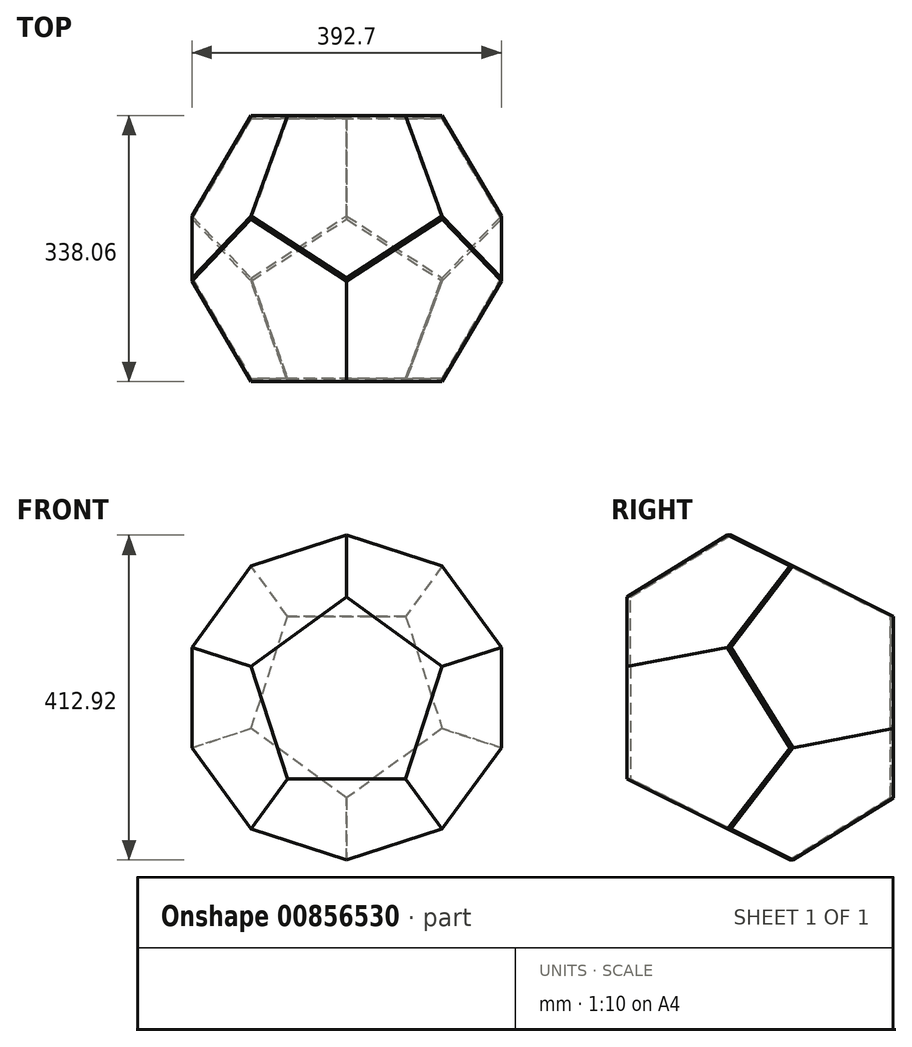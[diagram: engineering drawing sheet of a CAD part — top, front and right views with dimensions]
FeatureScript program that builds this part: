
annotation { "Feature Type Name" : "Feature", "Feature Type Description" : "" }
export const myFeature = defineFeature(function(context is Context, id is Id, definition is map)
    precondition{}
    {
        {
            var Q0;
            Q0=qCreatedBy(makeId("Front.planeOp"),FACE);
            var sketch = newSketch(context, id + "F0", { "sketchPlane" : qUnion([Q0])});
            skLineSegment(sketch, "E0", {"start": v(0, -103.23) * mm, "end": v(0, 127.6) * mm, "construction": true});
            skLineSegment(sketch, "E1", {"start": v(75, -103.23) * mm, "end": v(-75, -103.23) * mm});
            skLineSegment(sketch, "E2", {"start": v(0, -103.23) * mm, "end": v(0, 0) * mm, "construction": true});
            skLineSegment(sketch, "E3.1.0", {"start": v(121.35, 39.43) * mm, "end": v(75, -103.23) * mm});
            skLineSegment(sketch, "E3.2.0", {"start": v(0, 127.6) * mm, "end": v(121.35, 39.43) * mm});
            skLineSegment(sketch, "E3.3.0", {"start": v(-121.35, 39.43) * mm, "end": v(0, 127.6) * mm});
            skLineSegment(sketch, "E3.4.0", {"start": v(-75, -103.23) * mm, "end": v(-121.35, 39.43) * mm});
            skPoint(sketch, "E3.center", {"position": v(0, 0) * mm});
            skLineSegment(sketch, "E4", {"start": v(-121.35, 39.43) * mm, "end": v(98.18, -31.9) * mm, "construction": true});
            skLineSegment(sketch, "E5", {"start": v(-75, -103.23) * mm, "end": v(60.68, 83.51) * mm, "construction": true});
            skLineSegment(sketch, "E6", {"start": v(-60.68, 83.51) * mm, "end": v(75, -103.23) * mm, "construction": true});
            skLineSegment(sketch, "E7", {"start": v(121.35, 39.43) * mm, "end": v(-98.18, -31.9) * mm, "construction": true});
            skLineSegment(sketch, "E8.bottom", {"start": v(-75, -103.23) * mm, "end": v(75, -103.23) * mm, "construction": true});
            skLineSegment(sketch, "E8.top", {"start": v(-75, 103.23) * mm, "end": v(75, 103.23) * mm, "construction": true});
            skLineSegment(sketch, "E8.left", {"start": v(-75, -103.23) * mm, "end": v(-75, 103.23) * mm, "construction": true});
            skLineSegment(sketch, "E8.right", {"start": v(75, -103.23) * mm, "end": v(75, 103.23) * mm, "construction": true});
            skSolve(sketch);
        }
        {
            var Q0;
            Q0=qCreatedBy(makeId("Right.planeOp"),FACE);
            var sketch = newSketch(context, id + "F1", { "sketchPlane" : qUnion([Q0])});
            skLineSegment(sketch, "E9", {"start": v(0, -103.23) * mm, "end": v(60.48, -133.47) * mm, "construction": true});
            skSolve(sketch);
        }
        {
            var Q0;
            Q0=sQuery(id+"F1.wireOp",EDGE,"E9");
            var Q1;
            Q1=sQuery(id+"F0.wireOp",EDGE,"E1");
            cPlane(context, id + "F2", {"entities" : qUnion([Q0, Q1]), "cplaneType" : CPlaneType.LINE_ANGLE, "offset" : 25 * mm, "angle" : 0 * degree, "width" : 150 * mm, "height" : 150 * mm});
        }
        {
            var Q0;
            Q0=qCreatedBy(id+"F2.planeOp",FACE);
            var sketch = newSketch(context, id + "F3", { "sketchPlane" : qUnion([Q0])});
            skLineSegment(sketch, "E10.0", {"start": v(75, 46.17) * mm, "end": v(-75, 46.17) * mm});
            skLineSegment(sketch, "E11.1.0", {"start": v(121.35, 188.82) * mm, "end": v(75, 46.17) * mm});
            skLineSegment(sketch, "E11.2.0", {"start": v(0, 277) * mm, "end": v(121.35, 188.82) * mm});
            skLineSegment(sketch, "E11.3.0", {"start": v(-121.35, 188.82) * mm, "end": v(0, 277) * mm});
            skLineSegment(sketch, "E11.4.0", {"start": v(-75, 46.17) * mm, "end": v(-121.35, 188.82) * mm});
            skPoint(sketch, "E11.center", {"position": v(0, 149.4) * mm});
            skSolve(sketch);
        }
        {
            var Q0;
            Q0=sQuery(id+"F0.wireOp",EDGE,"E3.1.0");
            cPlane(context, id + "F4", {"entities" : qUnion([Q0]), "cplaneType" : CPlaneType.LINE_ANGLE, "offset" : 25 * mm, "angle" : 206.56 * degree, "width" : 150 * mm, "height" : 150 * mm});
        }
        {
            var Q0;
            Q0=qCreatedBy(id+"F4.planeOp",FACE);
            var sketch = newSketch(context, id + "F5", { "sketchPlane" : qUnion([Q0])});
            skLineSegment(sketch, "E12.0", {"start": v(46.17, 75) * mm, "end": v(46.17, -75) * mm});
            skLineSegment(sketch, "E13.1.0", {"start": v(46.17, -75) * mm, "end": v(188.82, -121.35) * mm});
            skLineSegment(sketch, "E13.2.0", {"start": v(188.82, -121.35) * mm, "end": v(277, 0) * mm});
            skLineSegment(sketch, "E13.3.0", {"start": v(277, 0) * mm, "end": v(188.82, 121.35) * mm});
            skLineSegment(sketch, "E13.4.0", {"start": v(188.82, 121.35) * mm, "end": v(46.17, 75) * mm});
            skPoint(sketch, "E13.center", {"position": v(149.4, 0) * mm});
            skSolve(sketch);
        }
        {
            var Q0;
            Q0=sQuery(id+"F0.wireOp",EDGE,"E3.2.0");
            var Q1;
            Q1=qCreatedBy(id+"FWBOnNek9pfn1HW_0.planeOp",FACE);
            cPlane(context, id + "F6", {"entities" : qUnion([Q0, Q1]), "cplaneType" : CPlaneType.LINE_ANGLE, "offset" : 25 * mm, "angle" : 116.56 * degree, "width" : 150 * mm, "height" : 150 * mm});
        }
        {
            var Q0;
            Q0=qCreatedBy(id+"F6.planeOp",FACE);
            var sketch = newSketch(context, id + "F7", { "sketchPlane" : qUnion([Q0])});
            skLineSegment(sketch, "E14.0", {"start": v(-57.06, 67.08) * mm, "end": v(85.6, 20.73) * mm});
            skLineSegment(sketch, "E15.1.0", {"start": v(85.6, 20.73) * mm, "end": v(173.76, 142.08) * mm});
            skLineSegment(sketch, "E15.2.0", {"start": v(173.76, 142.08) * mm, "end": v(85.6, 263.43) * mm});
            skLineSegment(sketch, "E15.3.0", {"start": v(85.6, 263.43) * mm, "end": v(-57.06, 217.08) * mm});
            skLineSegment(sketch, "E15.4.0", {"start": v(-57.06, 217.08) * mm, "end": v(-57.06, 67.08) * mm});
            skPoint(sketch, "E15.center", {"position": v(46.17, 142.08) * mm});
            skSolve(sketch);
        }
        {
            var Q0;
            Q0=sQuery(id+"F0.wireOp",VERTEX,"E1.end");
            var Q1;
            Q1=sQuery(id+"F3.wireOp",VERTEX,"E11.3.0.start");
            var Q2;
            Q2=sQuery(id+"F0.wireOp",VERTEX,"E3.3.0.start");
            cPlane(context, id + "F8", {"entities" : qUnion([Q0, Q1, Q2]), "cplaneType" : CPlaneType.THREE_POINT, "offset" : 25 * mm, "width" : 150 * mm, "height" : 150 * mm});
        }
        {
            var Q0;
            Q0=sQuery(id+"F0.wireOp",VERTEX,"E0.end");
            var Q1;
            Q1=sQuery(id+"F0.wireOp",VERTEX,"E3.3.0.start");
            var Q2;
            Q2=sQuery(id+"F7.wireOp",VERTEX,"E15.3.0.end");
            cPlane(context, id + "F9", {"entities" : qUnion([Q0, Q1, Q2]), "cplaneType" : CPlaneType.THREE_POINT, "offset" : 25 * mm, "width" : 150 * mm, "height" : 150 * mm});
        }
        {
            var Q0;
            Q0=qCreatedBy(id+"F8.planeOp",FACE);
            var sketch = newSketch(context, id + "F10", { "sketchPlane" : qUnion([Q0])});
            skLineSegment(sketch, "E16.0", {"start": v(-46.17, -75) * mm, "end": v(-46.17, 75) * mm});
            skLineSegment(sketch, "E17.1.0", {"start": v(-46.17, 75) * mm, "end": v(-188.82, 121.35) * mm});
            skLineSegment(sketch, "E17.2.0", {"start": v(-188.82, 121.35) * mm, "end": v(-277, 0) * mm});
            skLineSegment(sketch, "E17.3.0", {"start": v(-277, 0) * mm, "end": v(-188.82, -121.35) * mm});
            skLineSegment(sketch, "E17.4.0", {"start": v(-188.82, -121.35) * mm, "end": v(-46.17, -75) * mm});
            skPoint(sketch, "E17.center", {"position": v(-149.4, 0) * mm});
            skSolve(sketch);
        }
        {
            var Q0;
            Q0=qCreatedBy(id+"F9.planeOp",FACE);
            var sketch = newSketch(context, id + "F11", { "sketchPlane" : qUnion([Q0])});
            skLineSegment(sketch, "E18.0", {"start": v(-85.6, 20.73) * mm, "end": v(57.06, 67.08) * mm});
            skLineSegment(sketch, "E19.1.0", {"start": v(57.06, 67.08) * mm, "end": v(57.06, 217.08) * mm});
            skLineSegment(sketch, "E19.2.0", {"start": v(57.06, 217.08) * mm, "end": v(-85.6, 263.43) * mm});
            skLineSegment(sketch, "E19.3.0", {"start": v(-85.6, 263.43) * mm, "end": v(-173.76, 142.08) * mm});
            skLineSegment(sketch, "E19.4.0", {"start": v(-173.76, 142.08) * mm, "end": v(-85.6, 20.73) * mm});
            skPoint(sketch, "E19.center", {"position": v(-46.17, 142.08) * mm});
            skSolve(sketch);
        }
        {
            var Q0;
            Q0=qCreatedBy(makeId("Top.planeOp"),FACE);
            var sketch = newSketch(context, id + "F12", { "sketchPlane" : qUnion([Q0])});
            skLineSegment(sketch, "E20", {"start": v(0, 0) * mm, "end": v(0, 579.75) * mm, "construction": true});
            skSolve(sketch);
        }
        {
            var Q0;
            Q0=sQuery(id+"F10.wireOp",VERTEX,"E17.1.0.end");
            var Q1;
            Q1=sQuery(id+"F10.wireOp",VERTEX,"E17.2.0.end");
            var Q2;
            Q2=sQuery(id+"F11.wireOp",VERTEX,"E19.2.0.end");
            cPlane(context, id + "F13", {"entities" : qUnion([Q0, Q1, Q2]), "cplaneType" : CPlaneType.THREE_POINT, "offset" : 25 * mm, "width" : 150 * mm, "height" : 150 * mm});
        }
        {
            var Q0;
            Q0=qCreatedBy(id+"F13.planeOp",FACE);
            var sketch = newSketch(context, id + "F14", { "sketchPlane" : qUnion([Q0])});
            skLineSegment(sketch, "E21.0", {"start": v(-109.96, 121.35) * mm, "end": v(-21.8, 0) * mm});
            skPoint(sketch, "E21.1", {"position": v(-65.88, 60.68) * mm});
            skLineSegment(sketch, "E22.1.0", {"start": v(-252.62, 75) * mm, "end": v(-109.96, 121.35) * mm});
            skLineSegment(sketch, "E22.2.0", {"start": v(-252.62, -75) * mm, "end": v(-252.62, 75) * mm});
            skLineSegment(sketch, "E22.3.0", {"start": v(-109.96, -121.35) * mm, "end": v(-252.62, -75) * mm});
            skLineSegment(sketch, "E22.4.0", {"start": v(-21.8, 0) * mm, "end": v(-109.96, -121.35) * mm});
            skPoint(sketch, "E22.center", {"position": v(-149.4, 0) * mm});
            skSolve(sketch);
        }
        {
            var Q0;
            Q0=sQuery(id+"F10.wireOp",VERTEX,"E17.2.0.end");
            var Q1;
            Q1=sQuery(id+"F3.wireOp",VERTEX,"E11.2.0.start");
            var Q2;
            Q2=sQuery(id+"F3.wireOp",VERTEX,"E11.3.0.start");
            cPlane(context, id + "F15", {"entities" : qUnion([Q0, Q1, Q2]), "cplaneType" : CPlaneType.THREE_POINT, "offset" : 25 * mm, "width" : 150 * mm, "height" : 150 * mm});
        }
        {
            var Q0;
            Q0=qCreatedBy(id+"F15.planeOp",FACE);
            var sketch = newSketch(context, id + "F16", { "sketchPlane" : qUnion([Q0])});
            skLineSegment(sketch, "E23.0", {"start": v(-81.43, 142.08) * mm, "end": v(6.74, 20.73) * mm});
            skLineSegment(sketch, "E24.1.0", {"start": v(6.74, 20.73) * mm, "end": v(149.4, 67.08) * mm});
            skLineSegment(sketch, "E24.2.0", {"start": v(149.4, 67.08) * mm, "end": v(149.4, 217.08) * mm});
            skLineSegment(sketch, "E24.3.0", {"start": v(149.4, 217.08) * mm, "end": v(6.74, 263.43) * mm});
            skLineSegment(sketch, "E24.4.0", {"start": v(6.74, 263.43) * mm, "end": v(-81.43, 142.08) * mm});
            skPoint(sketch, "E24.center", {"position": v(46.17, 142.08) * mm});
            skSolve(sketch);
        }
        {
            var Q0;
            Q0=sQuery(id+"F3.wireOp",VERTEX,"E11.2.0.start");
            var Q1;
            Q1=sQuery(id+"F16.wireOp",VERTEX,"E24.2.0.end");
            var Q2;
            Q2=sQuery(id+"F3.wireOp",VERTEX,"E11.1.0.start");
            cPlane(context, id + "F17", {"entities" : qUnion([Q0, Q1, Q2]), "cplaneType" : CPlaneType.THREE_POINT, "offset" : 25 * mm, "width" : 150 * mm, "height" : 150 * mm});
        }
        {
            var Q0;
            Q0=qCreatedBy(id+"F17.planeOp",FACE);
            var sketch = newSketch(context, id + "F18", { "sketchPlane" : qUnion([Q0])});
            skLineSegment(sketch, "E25.0", {"start": v(-149.4, 67.08) * mm, "end": v(-6.74, 20.73) * mm});
            skLineSegment(sketch, "E26.1.0", {"start": v(-6.74, 20.73) * mm, "end": v(81.43, 142.08) * mm});
            skLineSegment(sketch, "E26.2.0", {"start": v(81.43, 142.08) * mm, "end": v(-6.74, 263.43) * mm});
            skLineSegment(sketch, "E26.3.0", {"start": v(-6.74, 263.43) * mm, "end": v(-149.4, 217.08) * mm});
            skLineSegment(sketch, "E26.4.0", {"start": v(-149.4, 217.08) * mm, "end": v(-149.4, 67.08) * mm});
            skPoint(sketch, "E26.center", {"position": v(-46.16, 142.08) * mm});
            skSolve(sketch);
        }
        {
            var Q0;
            Q0=sQuery(id+"F5.wireOp",VERTEX,"E13.2.0.end");
            var Q1;
            Q1=sQuery(id+"F5.wireOp",VERTEX,"E13.3.0.end");
            var Q2;
            Q2=sQuery(id+"F7.wireOp",VERTEX,"E15.2.0.end");
            cPlane(context, id + "F19", {"entities" : qUnion([Q0, Q1, Q2]), "cplaneType" : CPlaneType.THREE_POINT, "offset" : 25 * mm, "width" : 150 * mm, "height" : 150 * mm});
        }
        {
            var Q0;
            Q0=qCreatedBy(id+"F19.planeOp",FACE);
            var sketch = newSketch(context, id + "F20", { "sketchPlane" : qUnion([Q0])});
            skLineSegment(sketch, "E27.0", {"start": v(109.96, -121.35) * mm, "end": v(21.8, 0) * mm});
            skLineSegment(sketch, "E28.1.0", {"start": v(252.62, -75) * mm, "end": v(109.96, -121.35) * mm});
            skLineSegment(sketch, "E28.2.0", {"start": v(252.62, 75) * mm, "end": v(252.62, -75) * mm});
            skLineSegment(sketch, "E28.3.0", {"start": v(109.96, 121.35) * mm, "end": v(252.62, 75) * mm});
            skLineSegment(sketch, "E28.4.0", {"start": v(21.8, 0) * mm, "end": v(109.96, 121.35) * mm});
            skPoint(sketch, "E28.center", {"position": v(149.4, 0) * mm});
            skSolve(sketch);
        }
        {
            var Q0;
            Q0=sQuery(id+"F7.wireOp",VERTEX,"E15.2.0.end");
            var Q1;
            Q1=sQuery(id+"F11.wireOp",VERTEX,"E19.2.0.end");
            var Q2;
            Q2=sQuery(id+"F7.wireOp",VERTEX,"E15.3.0.end");
            cPlane(context, id + "F21", {"entities" : qUnion([Q0, Q1, Q2]), "cplaneType" : CPlaneType.THREE_POINT, "offset" : 25 * mm, "width" : 150 * mm, "height" : 150 * mm});
        }
        {
            var Q0;
            Q0=qCreatedBy(id+"F21.planeOp",FACE);
            var sketch = newSketch(context, id + "F22", { "sketchPlane" : qUnion([Q0])});
            skLineSegment(sketch, "E29.0", {"start": v(121.35, -109.96) * mm, "end": v(75, -252.62) * mm});
            skLineSegment(sketch, "E30.1.0", {"start": v(0, -21.8) * mm, "end": v(121.35, -109.96) * mm});
            skLineSegment(sketch, "E30.2.0", {"start": v(-121.35, -109.96) * mm, "end": v(0, -21.8) * mm});
            skLineSegment(sketch, "E30.3.0", {"start": v(-75, -252.62) * mm, "end": v(-121.35, -109.96) * mm});
            skLineSegment(sketch, "E30.4.0", {"start": v(75, -252.62) * mm, "end": v(-75, -252.62) * mm});
            skPoint(sketch, "E30.center", {"position": v(0, -149.4) * mm});
            skSolve(sketch);
        }
        {
            var Q0;
            Q0=sQuery(id+"F14.wireOp",VERTEX,"E22.1.0.start");
            var Q1;
            Q1=sQuery(id+"F18.wireOp",VERTEX,"E26.2.0.end");
            var Q2;
            Q2=sQuery(id+"F16.wireOp",VERTEX,"E24.2.0.end");
            cPlane(context, id + "F23", {"entities" : qUnion([Q0, Q1, Q2]), "cplaneType" : CPlaneType.THREE_POINT, "offset" : 25 * mm, "width" : 150 * mm, "height" : 150 * mm});
        }
        {
            var Q0;
            Q0=qCreatedBy(id+"F23.planeOp",FACE);
            var sketch = newSketch(context, id + "F24", { "sketchPlane" : qUnion([Q0])});
            skLineSegment(sketch, "E31.2", {"start": v(75, 103.23) * mm, "end": v(121.35, -39.43) * mm});
            skLineSegment(sketch, "E32.1.0", {"start": v(-75, 103.23) * mm, "end": v(75, 103.23) * mm});
            skLineSegment(sketch, "E32.2.0", {"start": v(-121.35, -39.43) * mm, "end": v(-75, 103.23) * mm});
            skLineSegment(sketch, "E32.3.0", {"start": v(0, -127.6) * mm, "end": v(-121.35, -39.43) * mm});
            skLineSegment(sketch, "E32.4.0", {"start": v(121.35, -39.43) * mm, "end": v(0, -127.6) * mm});
            skPoint(sketch, "E32.center", {"position": v(0, 0) * mm});
            skSolve(sketch);
        }
        {
            var Q0;
            Q0 = qSketchRegion(id + "F0", true);
            var Q1;
            Q1 = qSketchRegion(id + "F1", true);
            var Q2;
            Q2 = qSketchRegion(id + "F3", true);
            var Q3;
            Q3 = qSketchRegion(id + "F5", true);
            var Q4;
            Q4 = qSketchRegion(id + "F7", true);
            var Q5;
            Q5 = qSketchRegion(id + "F10", true);
            var Q6;
            Q6 = qSketchRegion(id + "F11", true);
            var Q7;
            Q7 = qSketchRegion(id + "F12", true);
            var Q8;
            Q8 = qSketchRegion(id + "F14", true);
            var Q9;
            Q9 = qSketchRegion(id + "F16", true);
            var Q10;
            Q10 = qSketchRegion(id + "F18", true);
            var Q11;
            Q11 = qSketchRegion(id + "F20", true);
            var Q12;
            Q12 = qSketchRegion(id + "F22", true);
            var Q13;
            Q13 = qSketchRegion(id + "F24", true);
            extrude(context, id + "F25", {"entities" : qUnion([Q0, Q1, Q2, Q3, Q4, Q5, Q6, Q7, Q8, Q9, Q10, Q11, Q12, Q13]), "endBound" : BoundingType.SYMMETRIC, "oppositeDirection" : true, "depth" : 4 * mm, "offsetDistance" : 25 * mm});
        }
    });
